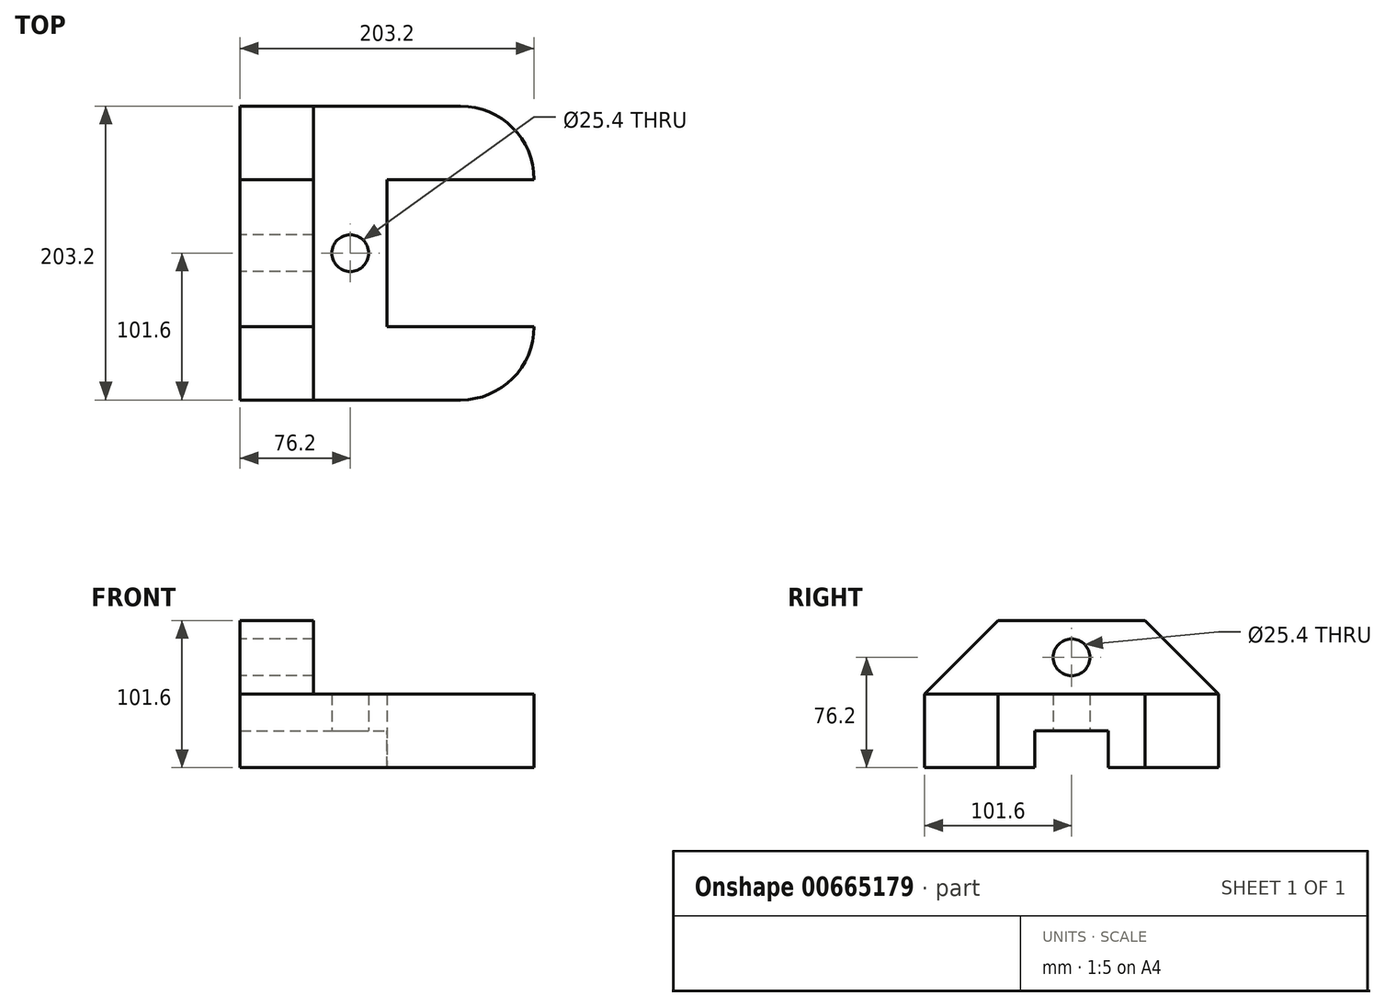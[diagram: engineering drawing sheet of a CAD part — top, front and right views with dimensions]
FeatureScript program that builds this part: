
annotation { "Feature Type Name" : "Feature", "Feature Type Description" : "" }
export const myFeature = defineFeature(function(context is Context, id is Id, definition is map)
    precondition{}
    {
        {
            var Q0;
            Q0=qCreatedBy(makeId("Top.planeOp"),FACE);
            var sketch = newSketch(context, id + "F0", { "sketchPlane" : qUnion([Q0])});
            skLineSegment(sketch, "E0", {"start": v(101.6, 152.4) * mm, "end": v(101.6, 50.8) * mm});
            skLineSegment(sketch, "E1", {"start": v(101.6, 50.8) * mm, "end": v(203.2, 50.8) * mm});
            skLineSegment(sketch, "E2", {"start": v(101.6, 152.4) * mm, "end": v(203.2, 152.4) * mm});
            skArc(sketch, "E3", {"start": v(152.4, 0) * mm, "mid": v(188.32, 14.88) * mm, "end": v(203.2, 50.8) * mm});
            skArc(sketch, "E4", {"start": v(203.2, 152.4) * mm, "mid": v(188.32, 188.32) * mm, "end": v(152.4, 203.2) * mm});
            skLineSegment(sketch, "E5", {"start": v(0, 203.2) * mm, "end": v(152.4, 203.2) * mm});
            skLineSegment(sketch, "E6", {"start": v(0, 0) * mm, "end": v(152.4, 0) * mm});
            skCircle(sketch, "E7", {"center": v(76.2, 101.6) * mm, "radius": 12.7 * mm});
            skLineSegment(sketch, "E8", {"start": v(0, 203.2) * mm, "end": v(0, 0) * mm});
            skLineSegment(sketch, "E9", {"start": v(76.2, 101.6) * mm, "end": v(101.6, 101.6) * mm, "construction": true});
            skSolve(sketch);
        }
        {
            var Q0;
            Q0=makeQuery(id+"F0.imprint","IMPRINT",FACE,{"disambiguationData":[TD([[makeQuery(id+"F0.imprint","IMPRINT",EDGE,{"derivedFrom":sQuery(id+"F0.wireOp",EDGE,"E0")}),-1.0]])]});
            extrude(context, id + "F1", {"entities" : qUnion([Q0]), "depth" : 50.8 * mm, "offsetDistance" : 25.4 * mm});
        }
        {
            var Q0;
            Q0=makeQuery(id+"F1.opExtrude","SWEPT_FACE",FACE,{"disambiguationData":[OSD([sQuery(id+"F0.wireOp",EDGE,"E8")])]});
            var sketch = newSketch(context, id + "F2", { "sketchPlane" : qUnion([Q0])});
            skLineSegment(sketch, "E10", {"start": v(-203.2, 50.8) * mm, "end": v(-152.4, 101.6) * mm});
            skLineSegment(sketch, "E11", {"start": v(-152.4, 101.6) * mm, "end": v(-50.8, 101.6) * mm});
            skLineSegment(sketch, "E12", {"start": v(-50.8, 101.6) * mm, "end": v(0, 50.8) * mm});
            skLineSegment(sketch, "E13", {"start": v(0, 50.8) * mm, "end": v(-203.2, 50.8) * mm});
            skLineSegment(sketch, "E14", {"start": v(-101.6, 50.8) * mm, "end": v(-101.6, 101.6) * mm, "construction": true});
            skCircle(sketch, "E15", {"center": v(-101.6, 76.2) * mm, "radius": 12.7 * mm});
            skSolve(sketch);
        }
        {
            var Q0;
            Q0=makeQuery(id+"F2.imprint","IMPRINT",FACE,{"disambiguationData":[TD([[makeQuery(id+"F2.imprint","IMPRINT",EDGE,{"derivedFrom":sQuery(id+"F2.wireOp",EDGE,"E10")}),-1.0]])]});
            extrude(context, id + "F3", {"entities" : qUnion([Q0]), "operationType" : NewBodyOperationType.ADD, "oppositeDirection" : true, "depth" : 50.8 * mm, "offsetDistance" : 25.4 * mm});
        }
        {
            var Q0;
            Q0=makeQuery(id+"F1.opExtrude","SWEPT_FACE",FACE,{"disambiguationData":[OSD([sQuery(id+"F0.wireOp",EDGE,"E0")])]});
            var sketch = newSketch(context, id + "F4", { "sketchPlane" : qUnion([Q0])});
            skLineSegment(sketch, "E16", {"start": v(76.2, 0) * mm, "end": v(76.2, 25.4) * mm});
            skLineSegment(sketch, "E17", {"start": v(76.2, 25.4) * mm, "end": v(127, 25.4) * mm});
            skLineSegment(sketch, "E18", {"start": v(127, 25.4) * mm, "end": v(127, 0) * mm});
            skLineSegment(sketch, "E19", {"start": v(127, 0) * mm, "end": v(76.2, 0) * mm});
            skSolve(sketch);
        }
        {
            var Q0;
            Q0=makeQuery(id+"F4.imprint","IMPRINT",FACE,{"disambiguationData":[TD([[makeQuery(id+"F4.imprint","IMPRINT",EDGE,{"derivedFrom":sQuery(id+"F4.wireOp",EDGE,"E16")}),-1.0]])]});
            extrude(context, id + "F5", {"entities" : qUnion([Q0]), "operationType" : NewBodyOperationType.REMOVE, "oppositeDirection" : true, "depth" : 101.6 * mm, "offsetDistance" : 25.4 * mm});
        }
    });
